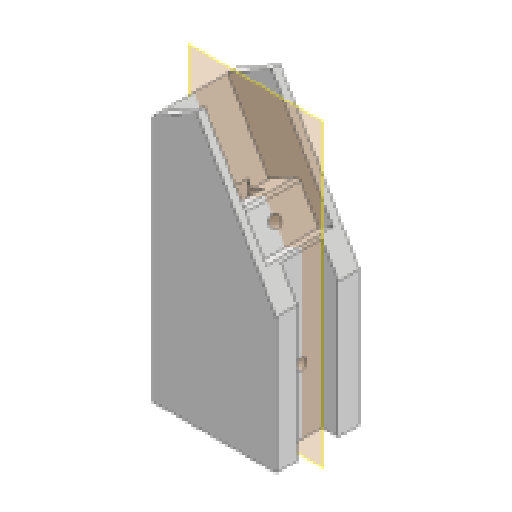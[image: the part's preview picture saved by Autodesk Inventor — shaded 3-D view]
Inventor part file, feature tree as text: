
AUTODESK INVENTOR PART (.ipt)
format: ipt  version: 2025.1 (Build 291241020, 241B)  size: 176,640 bytes
history: native  units: in
note: dims shown in document units (in); Inventor stores cm internally (conversion verified against a paired STEP export)
features: extrude x9, sketch x9, reference x8, other x8, plane x2, mirror x1, chamfer x1, projected_geometry x1
ambient origin geometry x8: Origin, YZ Plane, XZ Plane, XY Plane, X Axis, Y Axis, Z Axis, Center Point
bodies: Solid1 (feature_tree)
feature tree (39):
  extrude  "Extrusion1"  Depth=1.0in
  extrude  "Extrusion2"  Depth=3.0in
  plane  "Work Plane1"
  mirror  "Mirror1"
  extrude  "Extrusion3"  Depth=0.81in TaperAngle=0.0deg
  extrude  "Extrusion4"  Depth=0.5in
  extrude  "Extrusion5"  Depth=0.2in
  chamfer  "Chamfer1"  Distance=2.5625in
  extrude  "Extrusion6"  Depth=0.487in
  plane  "Work Plane2"
  extrude  "Extrusion7"  Depth=0.2in TaperAngle=45.0deg
  extrude  "Extrusion8"  Depth=0.3in TaperAngle=0.0deg
  extrude  "Extrusion9"  Depth=0.4in TaperAngle=0.0deg
  sketch  "Sketch1"  dims[d0=0.618in d1=1.0in]
  sketch  "Sketch2"  dims[d2=1.5in d3=3.0in]
  projected_geometry  "Projected Loop1"
  sketch  "Sketch3"  dims[d4=120.0deg d5=0.81in d6=0.0in]
  sketch  "Sketch4"  dims[d7=0.1in d8=0.0in d9=0.5in]
  reference  "Reference1"
  sketch  "Sketch5"  dims[d10=0.25in d11=0.2in d12=2.5625in d13=0.0in]
  sketch  "Sketch6"  dims[d14=0.6in d15=0.0in d16=0.487in]
  reference  "Reference2"
  reference  "Reference3"
  reference  "Reference4"
  sketch  "Sketch7"  dims[d17=0.2in d18=0.0in d19=0.04in d20=0.125in d21=45.0deg]
  sketch  "Sketch8"  dims[d22=0.14in d23=0.3in d24=0.0in]
  reference  "Reference5"
  reference  "Reference6"
  sketch  "Sketch9"  dims[d25=0.2in d26=0.4in d27=0.0in d28=0.6in d29=0.0in d30=0.6in d31=0.0in]
  reference  "Reference7"
  reference  "Reference8"
  parser-record x2  (decoder bookkeeping rows leaked as tree rows — omitted from the tree; the rows remain in map.json)
  other  "Finger Assem.iam"
  other  "KNUCKLE 2:1"
  other  "Servo Base:2"
  other  "Hand Assem.iam"
  other  "Palm:1"
  other  "Wrist Base:1"
note: 2 file-system paths scrubbed to <path> (originals preserved in map.json)
